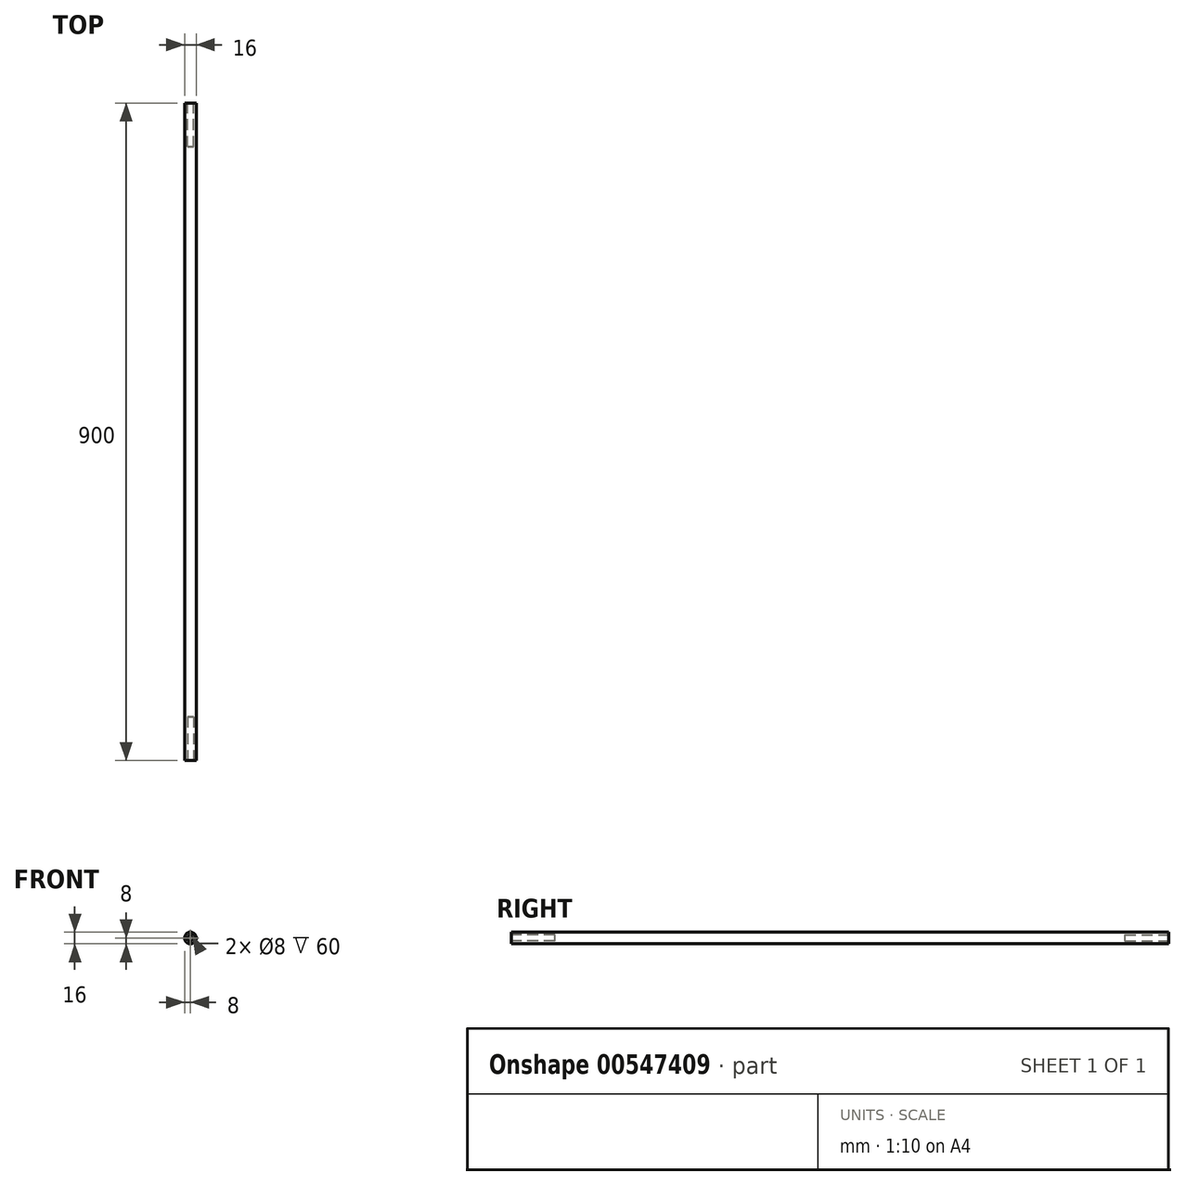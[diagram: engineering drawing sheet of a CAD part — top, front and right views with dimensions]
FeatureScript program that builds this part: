
annotation { "Feature Type Name" : "Feature", "Feature Type Description" : "" }
export const myFeature = defineFeature(function(context is Context, id is Id, definition is map)
    precondition{}
    {
        {
            var Q0;
            Q0=qCreatedBy(makeId("Front.planeOp"),FACE);
            var sketch = newSketch(context, id + "F0", { "sketchPlane" : qUnion([Q0])});
            skCircle(sketch, "E0", {"center": v(0, 0) * mm, "radius": 8 * mm});
            skSolve(sketch);
        }
        {
            var Q0;
            Q0 = qSketchRegion(id + "F0", true);
            extrude(context, id + "F1", {"entities" : qUnion([Q0]), "endBound" : BoundingType.SYMMETRIC, "depth" : 900 * mm, "offsetDistance" : 25 * mm});
        }
        {
            var Q0;
            Q0=makeQuery(id+"F1.opExtrude","CAP_FACE",FACE,{"disambiguationData":[OSD([sQuery(id+"F0.wireOp",EDGE,"E0")])],"isStart":false});
            var sketch = newSketch(context, id + "F2", { "sketchPlane" : qUnion([Q0])});
            skCircle(sketch, "E1", {"center": v(0, 0) * mm, "radius": 4 * mm});
            skSolve(sketch);
        }
        {
            var Q0;
            Q0 = qSketchRegion(id + "F2", true);
            extrude(context, id + "F3", {"entities" : qUnion([Q0]), "operationType" : NewBodyOperationType.REMOVE, "oppositeDirection" : true, "depth" : 60 * mm, "offsetDistance" : 25 * mm});
        }
        {
            var Q0;
            Q0=makeQuery(id+"F1.opExtrude","CAP_FACE",FACE,{"disambiguationData":[OSD([sQuery(id+"F0.wireOp",EDGE,"E0")])],"isStart":true});
            var sketch = newSketch(context, id + "F4", { "sketchPlane" : qUnion([Q0])});
            skCircle(sketch, "E2", {"center": v(0, 0) * mm, "radius": 4 * mm});
            skSolve(sketch);
        }
        {
            var Q0;
            Q0 = qSketchRegion(id + "F4", true);
            extrude(context, id + "F5", {"entities" : qUnion([Q0]), "operationType" : NewBodyOperationType.REMOVE, "oppositeDirection" : true, "depth" : 60 * mm, "offsetDistance" : 25 * mm});
        }
    });
